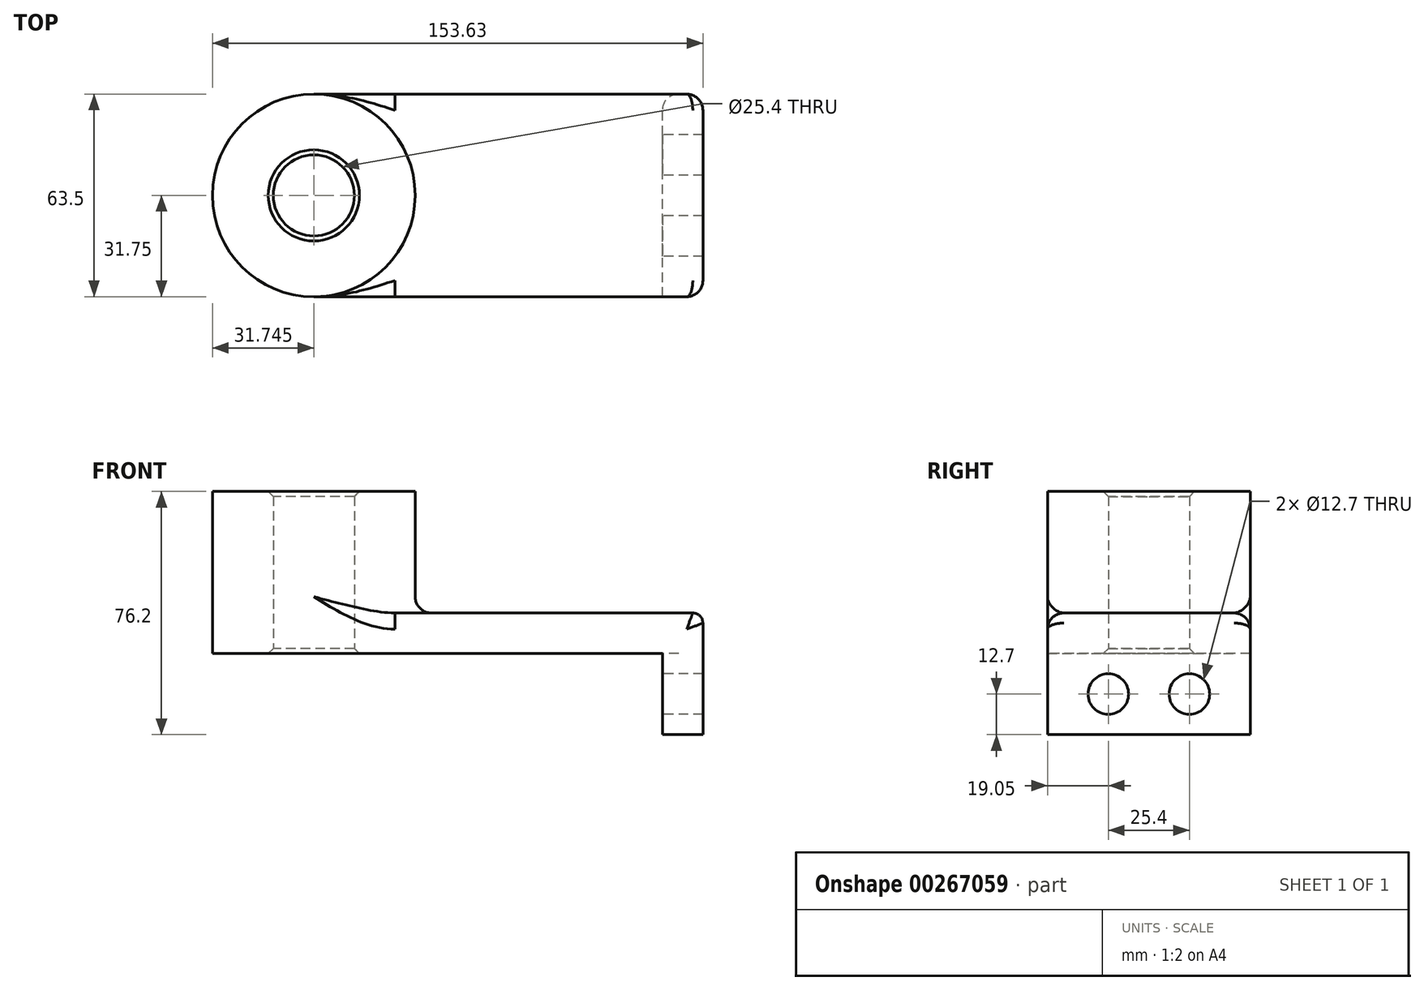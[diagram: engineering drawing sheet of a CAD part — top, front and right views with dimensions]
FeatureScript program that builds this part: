
annotation { "Feature Type Name" : "Feature", "Feature Type Description" : "" }
export const myFeature = defineFeature(function(context is Context, id is Id, definition is map)
    precondition{}
    {
        {
            var Q0;
            Q0=qCreatedBy(makeId("Top.planeOp"),FACE);
            var sketch = newSketch(context, id + "F0", { "sketchPlane" : qUnion([Q0])});
            skLineSegment(sketch, "E0.bottom", {"start": v(54.6, -31.75) * mm, "end": v(-54.6, -31.75) * mm});
            skLineSegment(sketch, "E0.top", {"start": v(54.6, 31.75) * mm, "end": v(-54.6, 31.75) * mm});
            skLineSegment(sketch, "E0.left", {"start": v(54.6, -31.75) * mm, "end": v(54.6, 31.75) * mm});
            skLineSegment(sketch, "E0.right", {"start": v(-54.6, -31.75) * mm, "end": v(-54.6, 31.75) * mm});
            skPoint(sketch, "E0.middle", {"position": v(0, 0) * mm});
            skCircle(sketch, "E1", {"center": v(-54.6, 0) * mm, "radius": 31.75 * mm});
            skCircle(sketch, "E2", {"center": v(-54.6, 0) * mm, "radius": 12.7 * mm});
            skSolve(sketch);
        }
        {
            var Q0;
            Q0 = qSketchRegion(id + "F0", true);
            extrude(context, id + "F1", {"entities" : qUnion([Q0]), "depth" : 12.7 * mm});
        }
        {
            var Q0;
            Q0=makeQuery(id+"F1.opExtrude","SWEPT_FACE",FACE,{"disambiguationData":[OSD([sQuery(id+"F0.wireOp",EDGE,"E0.left")])]});
            var sketch = newSketch(context, id + "F2", { "sketchPlane" : qUnion([Q0])});
            skLineSegment(sketch, "E3.bottom", {"start": v(-31.75, 12.7) * mm, "end": v(31.75, 12.7) * mm});
            skLineSegment(sketch, "E3.top", {"start": v(-31.75, -25.4) * mm, "end": v(31.75, -25.4) * mm});
            skLineSegment(sketch, "E3.left", {"start": v(-31.75, 12.7) * mm, "end": v(-31.75, -25.4) * mm});
            skLineSegment(sketch, "E3.right", {"start": v(31.75, 12.7) * mm, "end": v(31.75, -25.4) * mm});
            skCircle(sketch, "E4", {"center": v(-12.7, -12.7) * mm, "radius": 6.35 * mm});
            skLineSegment(sketch, "E5", {"start": v(0, 0) * mm, "end": v(0, -25.4) * mm, "construction": true});
            skCircle(sketch, "E6.MirrorC", {"center": v(12.7, -12.7) * mm, "radius": 6.35 * mm});
            skSolve(sketch);
        }
        {
            var Q0;
            Q0 = qSketchRegion(id + "F2", true);
            extrude(context, id + "F3", {"entities" : qUnion([Q0]), "operationType" : NewBodyOperationType.ADD, "depth" : 12.7 * mm});
        }
        {
            var Q0;
            Q0=makeQuery(id+"F3.opExtrude","CAP_EDGE",EDGE,{"disambiguationData":[OSD([sQuery(id+"F2.wireOp",EDGE,"E3.bottom")])],"isStart":false});
            fillet(context, id + "F4", {"entities" : qUnion([Q0]), "radius" : 3.17 * mm, "tangentPropagation" : true, "allowEdgeOverflow" : false});
        }
        {
            var Q0;
            {var subQ1=sQuery(id+"F0.wireOp",EDGE,"E0.right");var subQ3=sQuery(id+"F0.wireOp",EDGE,"E2");var subQ4=makeQuery(id+"F0.imprint","INTERSECT",VERTEX,{"disambiguationData":[OD(0.0)],"derivedFrom":[subQ1,subQ3]});Q0=makeQuery(id+"F0.imprint","IMPRINT",FACE,{"disambiguationData":[TD([[makeQuery(id+"F0.imprint","IMPRINT",EDGE,{"disambiguationData":[TD([[subQ4,1.0]])],"derivedFrom":subQ3}),-1.0]])]});}
            var Q1;
            {var subQ1=sQuery(id+"F0.wireOp",EDGE,"E0.right");var subQ3=sQuery(id+"F0.wireOp",EDGE,"E2");var subQ4=makeQuery(id+"F0.imprint","INTERSECT",VERTEX,{"disambiguationData":[OD(0.0)],"derivedFrom":[subQ1,subQ3]});Q1=makeQuery(id+"F0.imprint","IMPRINT",FACE,{"disambiguationData":[TD([[makeQuery(id+"F0.imprint","IMPRINT",EDGE,{"disambiguationData":[TD([[subQ4,-1.0]])],"derivedFrom":subQ3}),-1.0]])]});}
            extrude(context, id + "F5", {"entities" : qUnion([Q0, Q1]), "operationType" : NewBodyOperationType.ADD, "depth" : 50.8 * mm});
        }
        {
            var Q0;
            {var subQ0=sQuery(id+"F0.wireOp",EDGE,"E1");Q0=makeQuery(id+"F5.boolean.opBoolean","INTERSECT",EDGE,{"derivedFrom":[makeQuery(id+"F3.boolean.opBoolean","MERGE",FACE,{"derivedFrom":[makeQuery(id+"F1.opExtrude","CAP_FACE",FACE,{"disambiguationData":[OSD([sQuery(id+"F0.wireOp",EDGE,"E0.bottom"),sQuery(id+"F0.wireOp",EDGE,"E0.top"),sQuery(id+"F0.wireOp",EDGE,"E0.left"),subQ0,sQuery(id+"F0.wireOp",EDGE,"E2")])],"isStart":false}),makeQuery(id+"F3.opExtrude","SWEPT_FACE",FACE,{"disambiguationData":[OSD([sQuery(id+"F2.wireOp",EDGE,"E3.bottom")])]})]}),makeQuery(id+"F5.opExtrude","SWEPT_FACE",FACE,{"disambiguationData":[OSD([subQ0])]})]});}
            fillet(context, id + "F6", {"entities" : qUnion([Q0]), "radius" : 5.08 * mm, "tangentPropagation" : true, "allowEdgeOverflow" : false});
        }
        {
            var Q0;
            Q0=makeQuery(id+"F3.boolean.opBoolean","MERGE",EDGE,{"derivedFrom":[makeQuery(id+"F1.opExtrude","CAP_EDGE",EDGE,{"disambiguationData":[OSD([sQuery(id+"F0.wireOp",EDGE,"E0.top")])],"isStart":false}),makeQuery(id+"F3.opExtrude","SWEPT_EDGE",EDGE,{"disambiguationData":[OSD([sQuery(id+"F2.wireOp",EDGE,"E3.bottom"),sQuery(id+"F2.wireOp",EDGE,"E3.right")])]})]});
            var Q1;
            Q1=makeQuery(id+"F3.opExtrude","CAP_EDGE",EDGE,{"disambiguationData":[OSD([sQuery(id+"F2.wireOp",EDGE,"E3.right")])],"isStart":true});
            var Q2;
            Q2=makeQuery(id+"F1.opExtrude","CAP_EDGE",EDGE,{"disambiguationData":[OSD([sQuery(id+"F0.wireOp",EDGE,"E0.left")])],"isStart":true});
            fillet(context, id + "F7", {"entities" : qUnion([Q0, Q1, Q2]), "radius" : 5.08 * mm, "tangentPropagation" : true, "allowEdgeOverflow" : false});
        }
        {
            var Q0;
            Q0=makeQuery(id+"F3.boolean.opBoolean","MERGE",EDGE,{"derivedFrom":[makeQuery(id+"F1.opExtrude","CAP_EDGE",EDGE,{"disambiguationData":[OSD([sQuery(id+"F0.wireOp",EDGE,"E0.bottom")])],"isStart":false}),makeQuery(id+"F3.opExtrude","SWEPT_EDGE",EDGE,{"disambiguationData":[OSD([sQuery(id+"F2.wireOp",EDGE,"E3.bottom"),sQuery(id+"F2.wireOp",EDGE,"E3.left")])]})]});
            fillet(context, id + "F8", {"entities" : qUnion([Q0]), "radius" : 5.08 * mm, "tangentPropagation" : true, "allowEdgeOverflow" : false});
        }
        {
            var Q0;
            {var subQ0=sQuery(id+"F0.wireOp",EDGE,"E2");Q0=makeQuery(id+"F5.boolean.opBoolean","MERGE",FACE,{"derivedFrom":[makeQuery(id+"F1.opExtrude","SWEPT_FACE",FACE,{"disambiguationData":[OSD([subQ0])]}),makeQuery(id+"F5.opExtrude","SWEPT_FACE",FACE,{"disambiguationData":[OSD([subQ0])]})]});}
            chamfer(context, id + "F9", {"entities" : qUnion([Q0]), "width" : 1.59 * mm, "tangentPropagation" : true});
        }
    });
